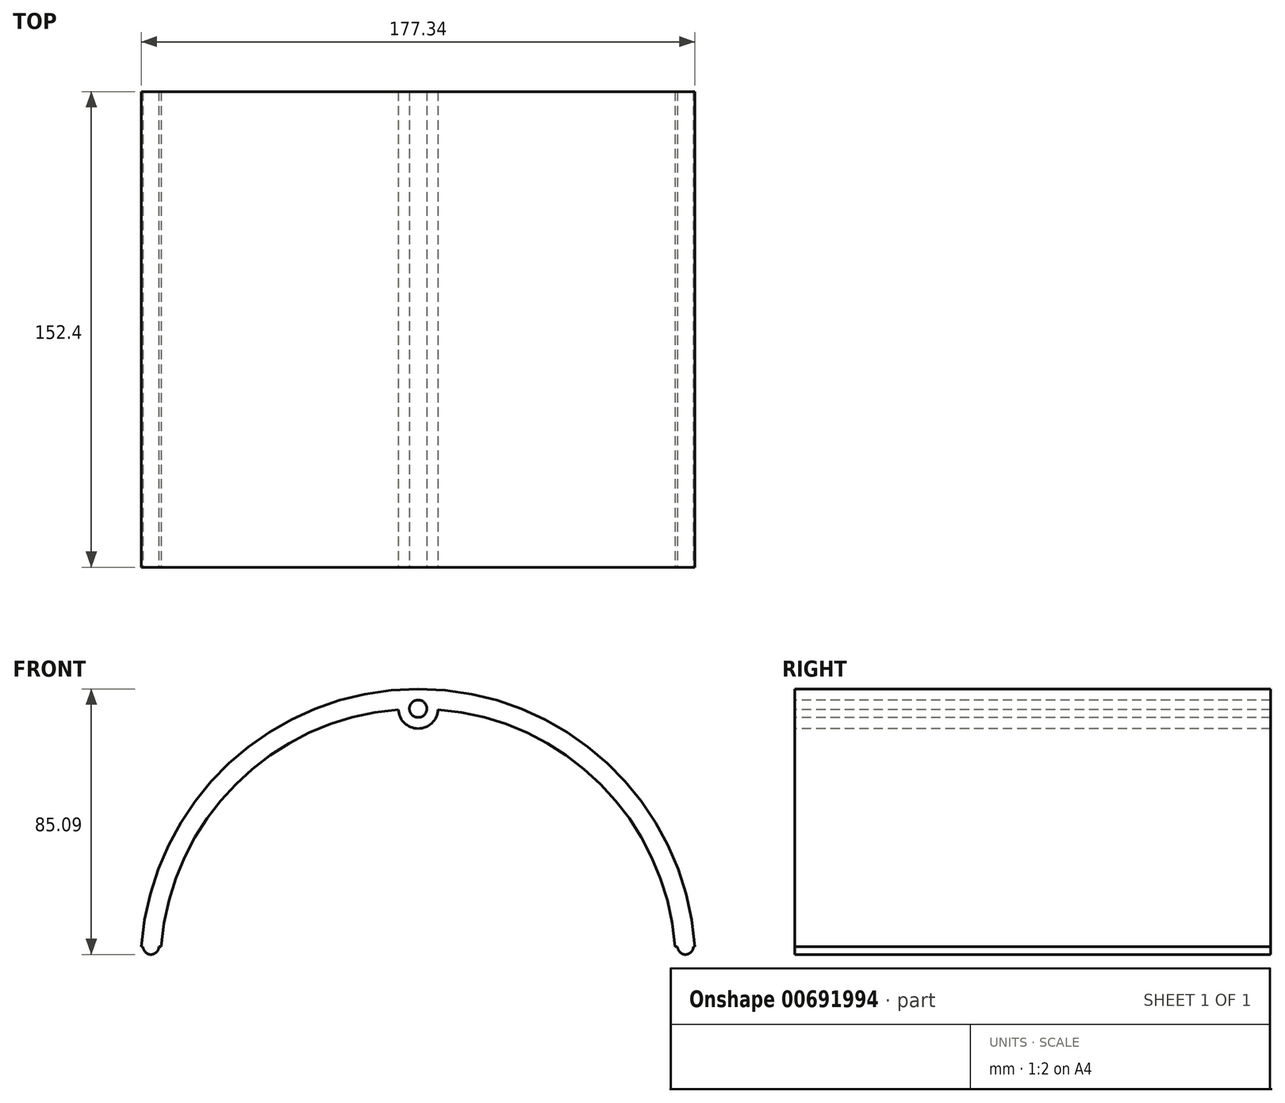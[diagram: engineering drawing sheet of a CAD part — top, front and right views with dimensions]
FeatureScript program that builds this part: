
annotation { "Feature Type Name" : "Feature", "Feature Type Description" : "" }
export const myFeature = defineFeature(function(context is Context, id is Id, definition is map)
    precondition{}
    {
        {
            var Q0;
            Q0=qCreatedBy(makeId("Front.planeOp"),FACE);
            var sketch = newSketch(context, id + "F0", { "sketchPlane" : qUnion([Q0])});
            skCircle(sketch, "E0", {"center": v(0, 0) * mm, "radius": 88.9 * mm});
            skSolve(sketch);
        }
        {
            var Q0;
            Q0=makeQuery(id+"F0.imprint","IMPRINT",FACE,{"disambiguationData":[TD([[makeQuery(id+"F0.imprint","IMPRINT",EDGE,{"derivedFrom":sQuery(id+"F0.wireOp",EDGE,"E0")}),1.0]])]});
            extrude(context, id + "F1", {"entities" : qUnion([Q0]), "oppositeDirection" : true, "depth" : 152.4 * mm, "offsetDistance" : 25.4 * mm});
        }
        {
            var Q0;
            Q0=makeQuery(id+"F1.opExtrude","CAP_FACE",FACE,{"disambiguationData":[OSD([sQuery(id+"F0.wireOp",EDGE,"E0")])],"isStart":true});
            var sketch = newSketch(context, id + "F2", { "sketchPlane" : qUnion([Q0])});
            skArc(sketch, "E1", {"start": v(2.8, -82.5) * mm, "mid": v(58.37, -58.37) * mm, "end": v(82.5, -2.8) * mm});
            skLineSegment(sketch, "E2", {"start": v(0, 0) * mm, "end": v(0, 79.76) * mm});
            skLineSegment(sketch, "E3", {"start": v(0, 0) * mm, "end": v(0, -79.76) * mm});
            skLineSegment(sketch, "E4", {"start": v(0, 0) * mm, "end": v(79.76, 0) * mm});
            skLineSegment(sketch, "E5", {"start": v(0, 0) * mm, "end": v(-79.76, 0) * mm});
            skCircle(sketch, "E6", {"center": v(0, 82.55) * mm, "radius": 2.8 * mm});
            skCircle(sketch, "E7", {"center": v(-82.55, 0) * mm, "radius": 2.8 * mm});
            skCircle(sketch, "E8", {"center": v(82.55, 0) * mm, "radius": 2.8 * mm});
            skCircle(sketch, "E9", {"center": v(0, -82.55) * mm, "radius": 2.8 * mm});
            skArc(sketch, "E10.trimOffspring", {"start": v(82.5, 2.8) * mm, "mid": v(58.37, 58.37) * mm, "end": v(2.8, 82.5) * mm});
            skArc(sketch, "E11.trimOffspring", {"start": v(-2.8, 82.5) * mm, "mid": v(-58.37, 58.37) * mm, "end": v(-82.5, 2.8) * mm});
            skArc(sketch, "E12.trimOffspring", {"start": v(-82.5, -2.8) * mm, "mid": v(-58.37, -58.37) * mm, "end": v(-2.8, -82.5) * mm});
            skSolve(sketch);
        }
        {
            var Q0;
            Q0=makeQuery(id+"F0.imprint","IMPRINT",FACE,{"disambiguationData":[TD([[makeQuery(id+"F0.imprint","IMPRINT",EDGE,{"derivedFrom":sQuery(id+"F0.wireOp",EDGE,"E0")}),1.0]])]});
            var sketch = newSketch(context, id + "F3", { "sketchPlane" : qUnion([Q0])});
            skCircle(sketch, "E13", {"center": v(0, 82.55) * mm, "radius": 6.35 * mm});
            skCircle(sketch, "E14", {"center": v(82.55, 0) * mm, "radius": 6.35 * mm});
            skCircle(sketch, "E15", {"center": v(-82.55, 0) * mm, "radius": 6.35 * mm});
            skCircle(sketch, "E16", {"center": v(0, -82.55) * mm, "radius": 6.35 * mm});
            skArc(sketch, "E17", {"start": v(-6.35, 82.3) * mm, "mid": v(-58.37, 58.37) * mm, "end": v(-82.3, 6.35) * mm});
            skArc(sketch, "E18.trimOffspring", {"start": v(82.3, 6.35) * mm, "mid": v(58.37, 58.37) * mm, "end": v(6.35, 82.3) * mm});
            skArc(sketch, "E19.trimOffspring", {"start": v(6.35, -82.3) * mm, "mid": v(58.37, -58.37) * mm, "end": v(82.3, -6.35) * mm});
            skArc(sketch, "E20.trimOffspring", {"start": v(-82.3, -6.35) * mm, "mid": v(-58.37, -58.37) * mm, "end": v(-6.35, -82.3) * mm});
            skSolve(sketch);
        }
        {
            var Q0;
            {var subQ0=sQuery(id+"F3.wireOp",EDGE,"E17");Q0=makeQuery(id+"F3.imprint","IMPRINT",FACE,{"disambiguationData":[TD([[makeQuery(id+"F3.imprint","IMPRINT",EDGE,{"derivedFrom":subQ0}),1.0]])]});}
            extrude(context, id + "F4", {"entities" : qUnion([Q0]), "operationType" : NewBodyOperationType.REMOVE, "endBound" : BoundingType.THROUGH_ALL, "oppositeDirection" : true, "depth" : 25.4 * mm, "offsetDistance" : 25.4 * mm});
        }
        {
            var Q0;
            {var subQ0=sQuery(id+"F2.wireOp",EDGE,"E6");var subQ1=makeQuery(id+"F2.imprint","INTERSECT",VERTEX,{"derivedFrom":[sQuery(id+"F2.wireOp",EDGE,"E2"),subQ0]});Q0=makeQuery(id+"F2.imprint","IMPRINT",FACE,{"disambiguationData":[TD([[makeQuery(id+"F2.imprint","IMPRINT",EDGE,{"disambiguationData":[TD([[subQ1,1.0]])],"derivedFrom":subQ0}),1.0]])]});}
            var Q1;
            {var subQ0=sQuery(id+"F2.wireOp",EDGE,"E7");var subQ1=makeQuery(id+"F2.imprint","INTERSECT",VERTEX,{"derivedFrom":[sQuery(id+"F2.wireOp",EDGE,"E5"),subQ0]});Q1=makeQuery(id+"F2.imprint","IMPRINT",FACE,{"disambiguationData":[TD([[makeQuery(id+"F2.imprint","IMPRINT",EDGE,{"disambiguationData":[TD([[subQ1,-1.0]])],"derivedFrom":subQ0}),1.0]])]});}
            var Q2;
            {var subQ0=sQuery(id+"F2.wireOp",EDGE,"E8");var subQ1=makeQuery(id+"F2.imprint","INTERSECT",VERTEX,{"derivedFrom":[sQuery(id+"F2.wireOp",EDGE,"E4"),subQ0]});Q2=makeQuery(id+"F2.imprint","IMPRINT",FACE,{"disambiguationData":[TD([[makeQuery(id+"F2.imprint","IMPRINT",EDGE,{"disambiguationData":[TD([[subQ1,1.0]])],"derivedFrom":subQ0}),1.0]])]});}
            var Q3;
            {var subQ0=sQuery(id+"F2.wireOp",EDGE,"E9");var subQ1=makeQuery(id+"F2.imprint","INTERSECT",VERTEX,{"derivedFrom":[sQuery(id+"F2.wireOp",EDGE,"E1"),subQ0]});Q3=makeQuery(id+"F2.imprint","IMPRINT",FACE,{"disambiguationData":[TD([[makeQuery(id+"F2.imprint","IMPRINT",EDGE,{"disambiguationData":[TD([[subQ1,-1.0]])],"derivedFrom":subQ0}),1.0]])]});}
            extrude(context, id + "F5", {"entities" : qUnion([Q0, Q1, Q2, Q3]), "operationType" : NewBodyOperationType.REMOVE, "endBound" : BoundingType.THROUGH_ALL, "oppositeDirection" : true, "depth" : 25.4 * mm, "offsetDistance" : 25.4 * mm});
        }
        {
            var Q0;
            {var subQ0=sQuery(id+"F3.wireOp",EDGE,"E17");Q0=makeQuery(id+"F3.imprint","IMPRINT",FACE,{"disambiguationData":[TD([[makeQuery(id+"F3.imprint","IMPRINT",EDGE,{"derivedFrom":subQ0}),1.0]])]});}
            var sketch = newSketch(context, id + "F6", { "sketchPlane" : qUnion([Q0])});
            skLineSegment(sketch, "E21", {"start": v(0, 0) * mm, "end": v(82.55, 0) * mm});
            skLineSegment(sketch, "E22", {"start": v(88.9, 0) * mm, "end": v(88.9, 6.35) * mm});
            skPoint(sketch, "E23.end.orphan", {"position": v(88.9, -97.1) * mm});
            skLineSegment(sketch, "E24", {"start": v(0, 0) * mm, "end": v(-88.9, 0) * mm});
            skLineSegment(sketch, "E25", {"start": v(-88.9, 0) * mm, "end": v(-88.9, 6.35) * mm});
            skLineSegment(sketch, "E26", {"start": v(-88.9, 6.35) * mm, "end": v(-88.14, 6.35) * mm});
            skLineSegment(sketch, "E27", {"start": v(-82.55, 6.35) * mm, "end": v(-83.06, 6.35) * mm});
            skCircle(sketch, "E28", {"center": v(-85.6, 6.35) * mm, "radius": 2.54 * mm});
            skLineSegment(sketch, "E29", {"start": v(88.9, 0) * mm, "end": v(82.55, 0) * mm});
            skLineSegment(sketch, "E30", {"start": v(82.55, 6.35) * mm, "end": v(83.06, 6.35) * mm});
            skCircle(sketch, "E31", {"center": v(85.6, 6.35) * mm, "radius": 2.54 * mm});
            skLineSegment(sketch, "E32", {"start": v(88.9, 0) * mm, "end": v(118.6, -139.2) * mm});
            skLineSegment(sketch, "E33", {"start": v(118.6, -139.2) * mm, "end": v(-105.38, -144.1) * mm});
            skLineSegment(sketch, "E34", {"start": v(-105.38, -144.1) * mm, "end": v(-88.9, 0) * mm});
            skLineSegment(sketch, "E35.trimOffspring", {"start": v(88.14, 6.35) * mm, "end": v(88.9, 6.35) * mm});
            skLineSegment(sketch, "E36.trimOffspring", {"start": v(-82.55, 6.35) * mm, "end": v(83.06, 6.35) * mm});
            skLineSegment(sketch, "E37", {"start": v(88.9, 6.35) * mm, "end": v(-109.31, 6.35) * mm});
            skLineSegment(sketch, "E38", {"start": v(-109.31, 6.35) * mm, "end": v(-104.9, -139.88) * mm});
            skLineSegment(sketch, "E39", {"start": v(-104.9, -139.88) * mm, "end": v(179.33, -117.08) * mm});
            skLineSegment(sketch, "E40", {"start": v(179.33, -117.08) * mm, "end": v(106.4, 6.35) * mm});
            skLineSegment(sketch, "E41", {"start": v(106.4, 6.35) * mm, "end": v(88.9, 6.35) * mm});
            skSolve(sketch);
        }
        {
            var Q0;
            {var subQ4=sQuery(id+"F6.wireOp",EDGE,"E29");Q0=makeQuery(id+"F6.imprint","IMPRINT",FACE,{"disambiguationData":[TD([[makeQuery(id+"F6.imprint","IMPRINT",EDGE,{"derivedFrom":subQ4}),1.0]])]});}
            var Q1;
            {var subQ4=sQuery(id+"F6.wireOp",EDGE,"E22");Q1=makeQuery(id+"F6.imprint","IMPRINT",FACE,{"disambiguationData":[TD([[makeQuery(id+"F6.imprint","IMPRINT",EDGE,{"derivedFrom":subQ4}),-1.0]])]});}
            var Q2;
            {var subQ5=sQuery(id+"F6.wireOp",EDGE,"E22");Q2=makeQuery(id+"F6.imprint","IMPRINT",FACE,{"disambiguationData":[TD([[makeQuery(id+"F6.imprint","IMPRINT",EDGE,{"derivedFrom":subQ5}),1.0]])]});}
            var Q3;
            {var subQ7=sQuery(id+"F6.wireOp",EDGE,"E25");Q3=makeQuery(id+"F6.imprint","IMPRINT",FACE,{"disambiguationData":[TD([[makeQuery(id+"F6.imprint","IMPRINT",EDGE,{"derivedFrom":subQ7}),-1.0]])]});}
            extrude(context, id + "F7", {"entities" : qUnion([Q0, Q1, Q2, Q3]), "operationType" : NewBodyOperationType.REMOVE, "endBound" : BoundingType.THROUGH_ALL, "oppositeDirection" : true, "depth" : 25.4 * mm, "offsetDistance" : 25.4 * mm});
        }
    });
